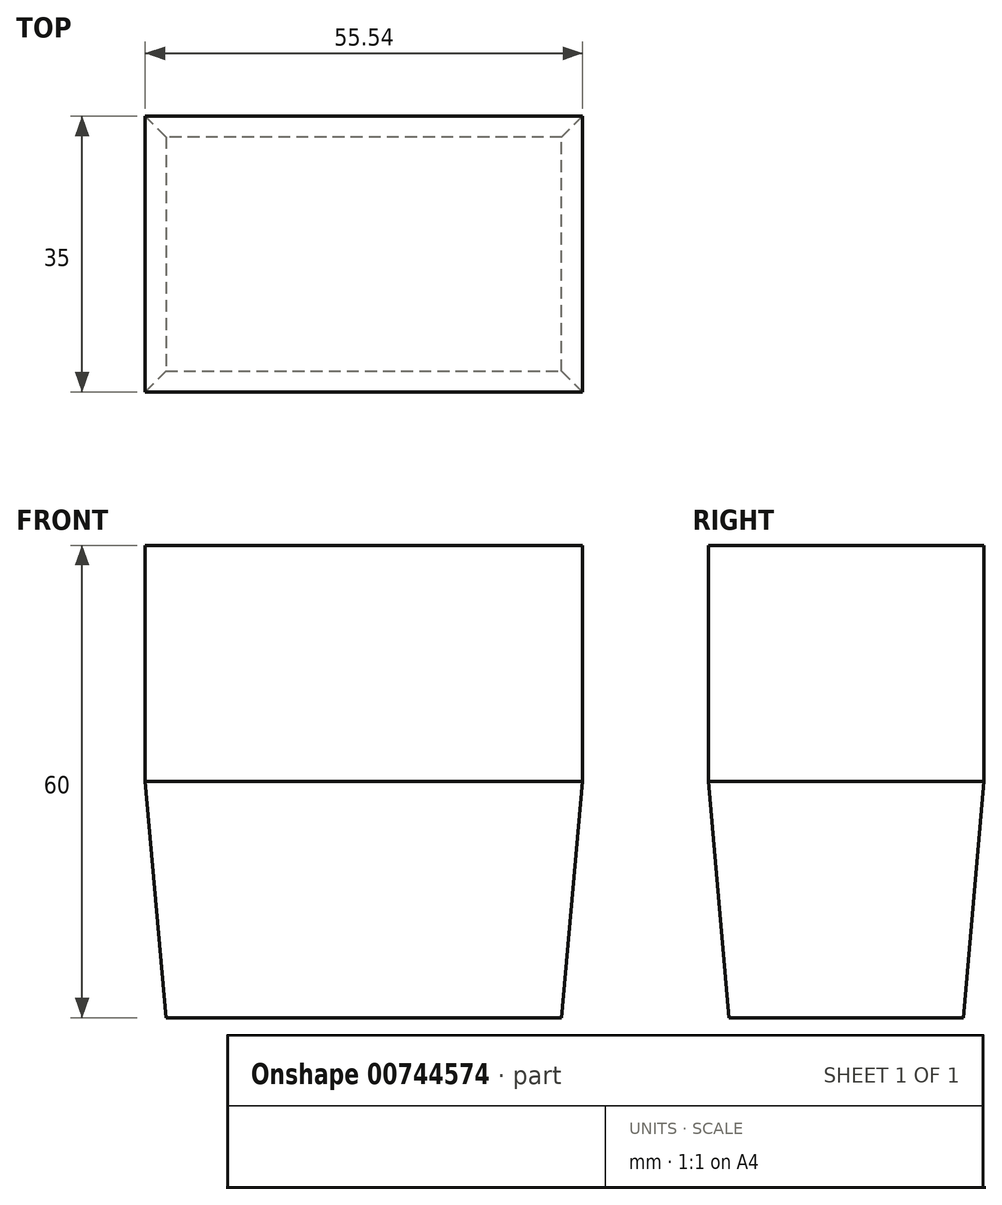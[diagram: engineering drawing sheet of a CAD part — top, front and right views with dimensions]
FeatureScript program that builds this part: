
annotation { "Feature Type Name" : "Feature", "Feature Type Description" : "" }
export const myFeature = defineFeature(function(context is Context, id is Id, definition is map)
    precondition{}
    {
        {
            var Q0;
            Q0=qCreatedBy(makeId("Front.planeOp"),FACE);
            var sketch = newSketch(context, id + "F0", { "sketchPlane" : qUnion([Q0])});
            skLineSegment(sketch, "E0.bottom", {"start": v(0, 0) * mm, "end": v(55.54, 0) * mm});
            skLineSegment(sketch, "E0.top", {"start": v(0, 30) * mm, "end": v(55.54, 30) * mm});
            skLineSegment(sketch, "E0.left", {"start": v(0, 0) * mm, "end": v(0, 30) * mm});
            skLineSegment(sketch, "E0.right", {"start": v(55.54, 0) * mm, "end": v(55.54, 30) * mm});
            skSolve(sketch);
        }
        {
            var Q0;
            Q0=qSketchRegion(id+"F0",true);
            extrude(context, id + "F1", {"entities" : qUnion([Q0]), "endBound" : BoundingType.SYMMETRIC, "depth" : 35 * mm, "offsetDistance" : 25 * mm});
        }
        {
            var Q0;
            Q0=makeQuery(id+"F1.opExtrude","SWEPT_FACE",FACE,{"disambiguationData":[OSD([sQuery(id+"F0.wireOp",EDGE,"E0.bottom")])]});
            extrude(context, id + "F2", {"entities" : qUnion([Q0]), "operationType" : NewBodyOperationType.ADD, "depth" : 30 * mm, "offsetDistance" : 25 * mm, "hasDraft" : true, "draftAngle" : 5 * degree, "draftPullDirection" : true});
        }
    });
